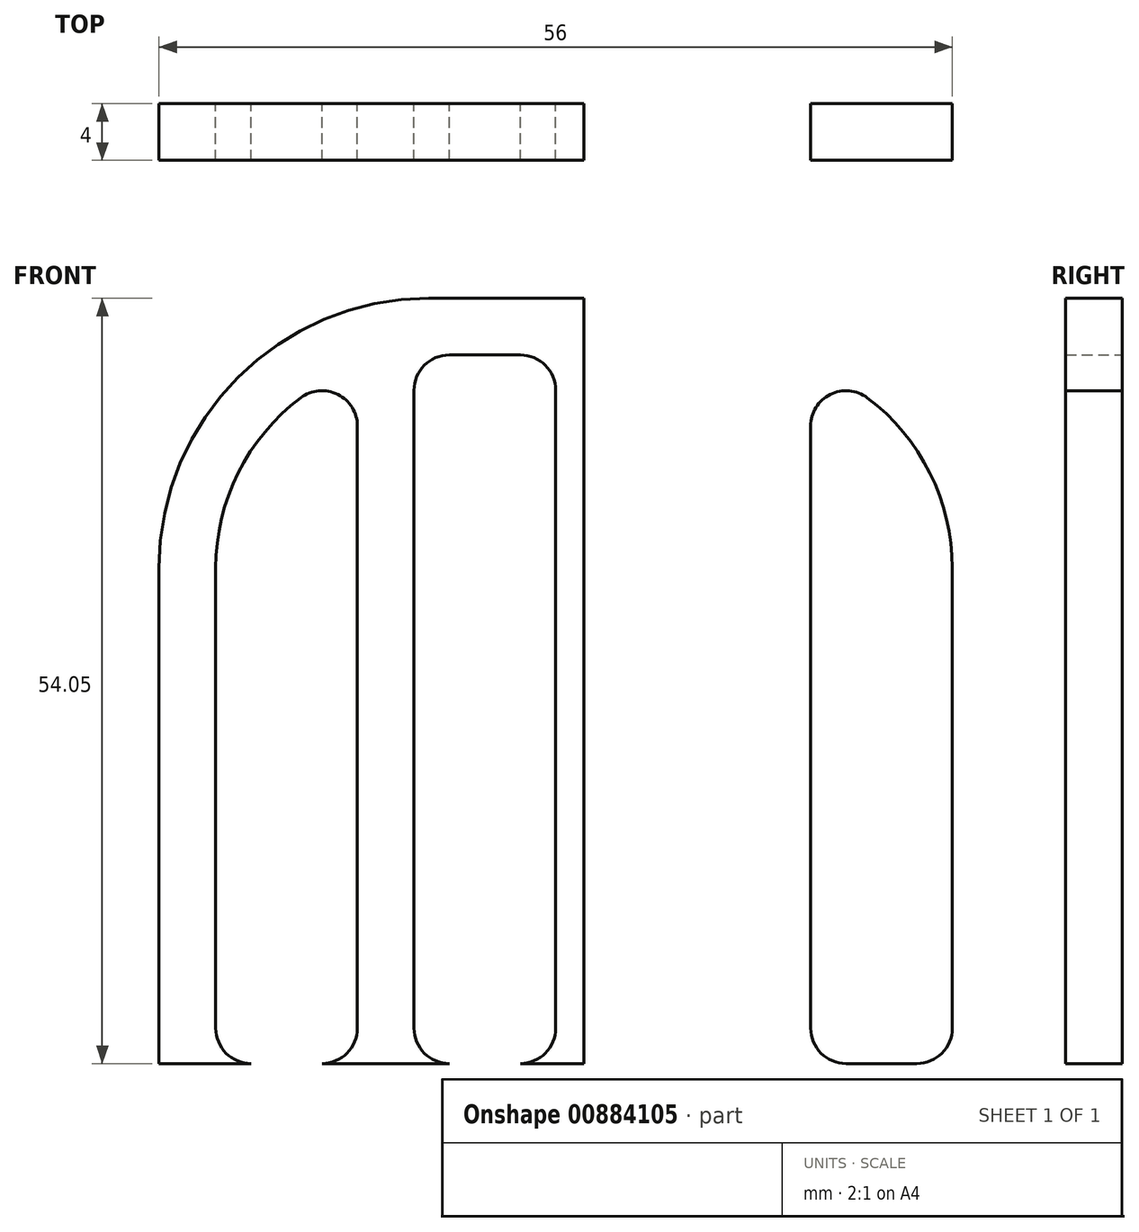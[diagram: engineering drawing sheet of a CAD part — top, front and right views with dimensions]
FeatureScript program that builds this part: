
annotation { "Feature Type Name" : "Feature", "Feature Type Description" : "" }
export const myFeature = defineFeature(function(context is Context, id is Id, definition is map)
    precondition{}
    {
        {
            var Q0;
            Q0=qCreatedBy(makeId("Front.planeOp"),FACE);
            var sketch = newSketch(context, id + "F0", { "sketchPlane" : qUnion([Q0])});
            skLineSegment(sketch, "E0.bottom", {"start": v(0, 0) * mm, "end": v(-30, 0) * mm});
            skLineSegment(sketch, "E0.top", {"start": v(0, 54.05) * mm, "end": v(-10.95, 54.05) * mm});
            skLineSegment(sketch, "E0.left", {"start": v(0, 0) * mm, "end": v(0, 54.05) * mm});
            skLineSegment(sketch, "E0.right", {"start": v(-30, 0) * mm, "end": v(-30, 35) * mm});
            skPoint(sketch, "E1.visualSharp", {"position": v(-30, 54.05) * mm});
            skArc(sketch, "E1.filletArc", {"start": v(-10.95, 54.05) * mm, "mid": v(-24.42, 48.47) * mm, "end": v(-30, 35) * mm});
            skLineSegment(sketch, "E2.bottom", {"start": v(-23.5, 0) * mm, "end": v(-18.5, 0) * mm});
            skLineSegment(sketch, "E2.left", {"start": v(-26, 2.5) * mm, "end": v(-26, 35) * mm});
            skLineSegment(sketch, "E2.right", {"start": v(-16, 2.5) * mm, "end": v(-16, 35) * mm});
            skLineSegment(sketch, "E3.bottom", {"start": v(-9.5, 0) * mm, "end": v(-4.5, 0) * mm});
            skLineSegment(sketch, "E3.top", {"start": v(-9.5, 50.05) * mm, "end": v(-4.5, 50.05) * mm});
            skLineSegment(sketch, "E3.left", {"start": v(-12, 2.5) * mm, "end": v(-12, 47.55) * mm});
            skLineSegment(sketch, "E3.right", {"start": v(-2, 2.5) * mm, "end": v(-2, 47.55) * mm});
            skLineSegment(sketch, "E4", {"start": v(-16, 35) * mm, "end": v(-16, 45.02) * mm});
            skArc(sketch, "E5", {"start": v(-20, 47.02) * mm, "mid": v(-24.42, 41.72) * mm, "end": v(-26, 35) * mm});
            skPoint(sketch, "E6.visualSharp", {"position": v(-12, 50.05) * mm});
            skArc(sketch, "E6.filletArc", {"start": v(-9.5, 50.05) * mm, "mid": v(-11.27, 49.32) * mm, "end": v(-12, 47.55) * mm});
            skPoint(sketch, "E7.visualSharp", {"position": v(-2, 50.05) * mm});
            skArc(sketch, "E7.filletArc", {"start": v(-2, 47.55) * mm, "mid": v(-2.73, 49.32) * mm, "end": v(-4.5, 50.05) * mm});
            skPoint(sketch, "E8.visualSharp", {"position": v(-16, 49.18) * mm});
            skArc(sketch, "E8.filletArc", {"start": v(-16, 45.02) * mm, "mid": v(-17.38, 47.26) * mm, "end": v(-20, 47.02) * mm});
            skPoint(sketch, "E9.visualSharp", {"position": v(-26, 0) * mm});
            skArc(sketch, "E9.filletArc", {"start": v(-26, 2.5) * mm, "mid": v(-25.27, 0.73) * mm, "end": v(-23.5, 0) * mm});
            skPoint(sketch, "E10.visualSharp", {"position": v(-16, 0) * mm});
            skArc(sketch, "E10.filletArc", {"start": v(-18.5, 0) * mm, "mid": v(-16.73, 0.73) * mm, "end": v(-16, 2.5) * mm});
            skPoint(sketch, "E11.visualSharp", {"position": v(-12, 0) * mm});
            skArc(sketch, "E11.filletArc", {"start": v(-12, 2.5) * mm, "mid": v(-11.27, 0.73) * mm, "end": v(-9.5, 0) * mm});
            skPoint(sketch, "E12.visualSharp", {"position": v(-2, 0) * mm});
            skArc(sketch, "E12.filletArc", {"start": v(-4.5, 0) * mm, "mid": v(-2.73, 0.73) * mm, "end": v(-2, 2.5) * mm});
            skArc(sketch, "E13.MirrorCS", {"start": v(18.5, 0) * mm, "mid": v(16.73, 0.73) * mm, "end": v(16, 2.5) * mm});
            skArc(sketch, "E14.MirrorCS", {"start": v(26, 2.5) * mm, "mid": v(25.27, 0.73) * mm, "end": v(23.5, 0) * mm});
            skArc(sketch, "E15.MirrorCS", {"start": v(12, 2.5) * mm, "mid": v(11.27, 0.73) * mm, "end": v(9.5, 0) * mm});
            skArc(sketch, "E16.MirrorCS", {"start": v(9.5, 50.05) * mm, "mid": v(11.27, 49.32) * mm, "end": v(12, 47.55) * mm});
            skArc(sketch, "E17.MirrorCS", {"start": v(4.5, 0) * mm, "mid": v(2.73, 0.73) * mm, "end": v(2, 2.5) * mm});
            skArc(sketch, "E18.MirrorCS", {"start": v(2, 47.55) * mm, "mid": v(2.73, 49.32) * mm, "end": v(4.5, 50.05) * mm});
            skPoint(sketch, "E19.MirrorP", {"position": v(30, 54.05) * mm});
            skLineSegment(sketch, "E20.MirrorCS", {"start": v(0, 0) * mm, "end": v(30, 0) * mm});
            skLineSegment(sketch, "E21.MirrorCS", {"start": v(0, 54.05) * mm, "end": v(10.95, 54.05) * mm});
            skPoint(sketch, "E22.MirrorP", {"position": v(2, 50.05) * mm});
            skArc(sketch, "E23.MirrorCS", {"start": v(16, 45.02) * mm, "mid": v(17.38, 47.26) * mm, "end": v(20, 47.02) * mm});
            skLineSegment(sketch, "E24.MirrorCS", {"start": v(23.5, 0) * mm, "end": v(18.5, 0) * mm});
            skLineSegment(sketch, "E25.MirrorCS", {"start": v(26, 2.5) * mm, "end": v(26, 35) * mm});
            skArc(sketch, "E26.MirrorCS", {"start": v(20, 47.02) * mm, "mid": v(24.42, 41.72) * mm, "end": v(26, 35) * mm});
            skLineSegment(sketch, "E27.MirrorCS", {"start": v(2, 2.5) * mm, "end": v(2, 47.55) * mm});
            skPoint(sketch, "E28.MirrorP", {"position": v(16, 49.18) * mm});
            skLineSegment(sketch, "E29.MirrorCS", {"start": v(16, 35) * mm, "end": v(16, 45.02) * mm});
            skPoint(sketch, "E30.MirrorP", {"position": v(12, 50.05) * mm});
            skPoint(sketch, "E31.MirrorP", {"position": v(12, 0) * mm});
            skPoint(sketch, "E32.MirrorP", {"position": v(16, 0) * mm});
            skLineSegment(sketch, "E33.MirrorCS", {"start": v(16, 2.5) * mm, "end": v(16, 35) * mm});
            skArc(sketch, "E34.MirrorCS", {"start": v(10.95, 54.05) * mm, "mid": v(24.42, 48.47) * mm, "end": v(30, 35) * mm});
            skLineSegment(sketch, "E35.MirrorCS", {"start": v(12, 2.5) * mm, "end": v(12, 47.55) * mm});
            skLineSegment(sketch, "E36.MirrorCS", {"start": v(30, 0) * mm, "end": v(30, 35) * mm});
            skPoint(sketch, "E37.MirrorP", {"position": v(2, 0) * mm});
            skLineSegment(sketch, "E38.MirrorCS", {"start": v(9.5, 50.05) * mm, "end": v(4.5, 50.05) * mm});
            skLineSegment(sketch, "E39.MirrorCS", {"start": v(9.5, 0) * mm, "end": v(4.5, 0) * mm});
            skPoint(sketch, "E40.MirrorP", {"position": v(26, 0) * mm});
            skSolve(sketch);
        }
        {
            var Q0;
            Q0=makeQuery(id+"F0.imprint","IMPRINT",FACE,{"disambiguationData":[TD([[makeQuery(id+"F0.imprint","IMPRINT",EDGE,{"derivedFrom":sQuery(id+"F0.wireOp",EDGE,"E0.top")}),1.0]])]});
            var Q1;
            {var subQ4=sQuery(id+"F0.wireOp",EDGE,"E13.MirrorCS");Q1=makeQuery(id+"F0.imprint","IMPRINT",FACE,{"disambiguationData":[TD([[makeQuery(id+"F0.imprint","IMPRINT",EDGE,{"derivedFrom":subQ4}),1.0]])]});}
            extrude(context, id + "F1", {"entities" : qUnion([Q0, Q1]), "depth" : 4 * mm, "offsetDistance" : 25 * mm});
        }
    });
